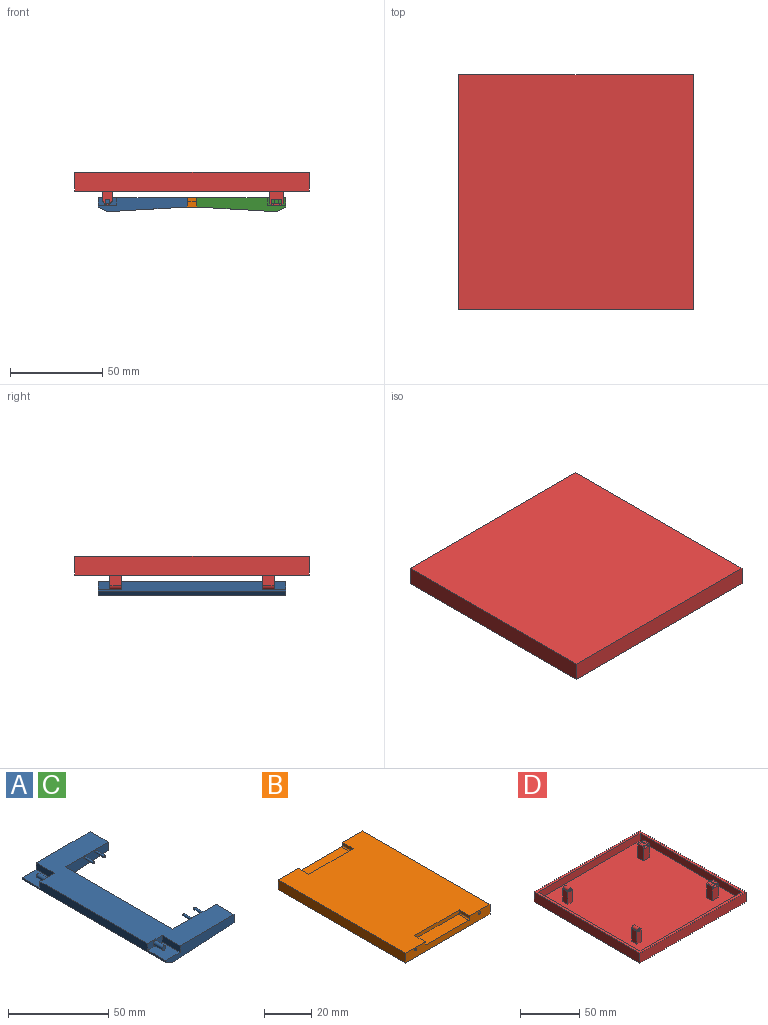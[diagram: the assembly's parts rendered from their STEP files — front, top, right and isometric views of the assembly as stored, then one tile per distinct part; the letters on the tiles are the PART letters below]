
ASSEMBLY  parts=4 mates=4
PART A: 29 faces, bbox 48.3x101.6x7.6 mm
  f0: plane 101.6x48.26mm, normal (0,0,1), area 2322.6mm2, adj f1,f2,f3,f4,f6,f8,f9,f10
  f1: plane 101.6x5.08mm, normal (-1,0,0), area 412.9mm2, adj f0,f2,f3,f7,f12,f13,f21,f22
  f2: plane 48.26x7.62mm, normal (0,1,0), area 265.2mm2, adj f0,f1,f5,f6,f7,f20,f21
  f3: plane 48.26x7.62mm, normal (0,-1,0), area 265.2mm2, adj f0,f1,f4,f5,f7,f11,f12
  f4: plane 12.7x5.08mm, normal (1,0,0), area 64.5mm2, adj f0,f3,f5,f8
  f5: plane 101.6x43.18mm, normal (0.06,0,-1), area 2068.1mm2, adj f2,f3,f4,f6,f7,f8,f9,f10
  f6: plane 12.7x5.08mm, normal (1,0,0), area 64.5mm2, adj f0,f2,f5,f9
  f7: plane 101.6x5.08mm, normal (-0.45,0,-0.89), area 577mm2, adj f1,f2,f3,f5
  f8: plane 30.48x6.87mm, normal (0,1,0), area 179.6mm2, adj f0,f4,f5,f10,f25,f27
  f9: plane 30.48x6.87mm, normal (0,-1,0), area 179.6mm2, adj f0,f5,f6,f10,f16,f18
  f10: plane 76.2x6.87mm, normal (1,0,0), area 523.7mm2, adj f0,f5,f8,f9
  f11: plane 12.7x4.06mm, normal (-1,0,0), area 51.6mm2, adj f0,f3,f12,f13
  f12: plane 12.7x10.16mm, normal (0,0,1), area 129mm2, adj f1,f3,f11,f13
  f13: plane 10.16x4.06mm, normal (0,-1,0), area 36.2mm2, adj f0,f1,f11,f12,f14
  f14: cylinder r=1.27mm len=6.35mm, axis (0,1,0), area 50.7mm2, adj f13,f15
  f15: plane 2.54x2.54mm, normal (0,-1,0), area 5.1mm2, adj f14
  f16: cylinder r=0.64mm len=6.35mm, axis (0,1,0), area 25.3mm2, adj f9,f17
  f17: plane 1.27x1.27mm, normal (0,-1,0), area 1.3mm2, adj f16
  f18: cylinder r=0.64mm len=6.35mm, axis (0,1,0), area 25.3mm2, adj f9,f19
  f19: plane 1.27x1.27mm, normal (0,-1,0), area 1.3mm2, adj f18
  f20: plane 12.7x4.06mm, normal (-1,0,0), area 51.6mm2, adj f0,f2,f21,f22
  f21: plane 12.7x10.16mm, normal (0,0,1), area 129mm2, adj f1,f2,f20,f22
  f22: plane 10.16x4.06mm, normal (0,1,0), area 36.2mm2, adj f0,f1,f20,f21,f23
  f23: cylinder r=1.27mm len=6.35mm, axis (0,-1,0), area 50.7mm2, adj f22,f24
  f24: plane 2.54x2.54mm, normal (0,1,0), area 5.1mm2, adj f23
  f25: cylinder r=0.64mm len=6.35mm, axis (0,-1,0), area 25.3mm2, adj f8,f26
  f26: plane 1.27x1.27mm, normal (0,1,0), area 1.3mm2, adj f25
  f27: cylinder r=0.64mm len=6.35mm, axis (0,-1,0), area 25.3mm2, adj f8,f28
  f28: plane 1.27x1.27mm, normal (0,1,0), area 1.3mm2, adj f27
PART B: 26 faces, bbox 50.8x76.2x5.1 mm
  f0: plane 50.8x5.08mm, normal (0,1,0), area 204.9mm2, adj f2,f3,f4,f5,f16,f17,f18,f19
  f1: plane 50.8x5.08mm, normal (0,-1,0), area 204.9mm2, adj f2,f3,f4,f5,f6,f7,f8,f9
  f2: plane 76.2x50.8mm, normal (0,0,-1), area 3871mm2, adj f0,f1,f3,f5
  f3: plane 76.2x5.08mm, normal (1,0,0), area 387.1mm2, adj f0,f1,f2,f4
  f4: plane 76.2x50.8mm, normal (0,0,1), area 3532.3mm2, adj f0,f1,f3,f5,f6,f10,f11,f16
  f5: plane 76.2x5.08mm, normal (-1,0,0), area 387.1mm2, adj f0,f1,f2,f4
  f6: plane 6.35x1.27mm, normal (1,0,0), area 8.1mm2, adj f1,f4,f7,f11
  f7: cylinder r=0.64mm len=6.35mm, axis (0,-1,0), area 6.3mm2, adj f1,f6,f8,f11
  f8: plane 25.4x6.35mm, normal (0,0,1), area 161.3mm2, adj f1,f7,f9,f11
  f9: cylinder r=0.64mm len=6.35mm, axis (0,-1,0), area 6.3mm2, adj f1,f8,f10,f11
  f10: plane 6.35x1.27mm, normal (-1,0,0), area 8.1mm2, adj f1,f4,f9,f11
  f11: plane 26.67x1.91mm, normal (0,-1,0), area 50.6mm2, adj f4,f6,f7,f8,f9,f10
  f12: cylinder r=0.64mm len=6.35mm, axis (0,-1,0), area 25.3mm2, adj f1,f13
  f13: plane 1.27x1.27mm, normal (0,-1,0), area 1.3mm2, adj f12
  f14: cylinder r=0.64mm len=6.35mm, axis (0,-1,0), area 25.3mm2, adj f1,f15
  f15: plane 1.27x1.27mm, normal (0,-1,0), area 1.3mm2, adj f14
  f16: plane 6.35x1.27mm, normal (1,0,0), area 8.1mm2, adj f0,f4,f20,f21
  f17: plane 6.35x1.27mm, normal (-1,0,0), area 8.1mm2, adj f0,f4,f18,f21
  f18: cylinder r=0.64mm len=6.35mm, axis (0,1,0), area 6.3mm2, adj f0,f17,f19,f21
  f19: plane 25.4x6.35mm, normal (0,0,1), area 161.3mm2, adj f0,f18,f20,f21
  f20: cylinder r=0.64mm len=6.35mm, axis (0,1,0), area 6.3mm2, adj f0,f16,f19,f21
  f21: plane 26.67x1.91mm, normal (0,1,0), area 50.6mm2, adj f4,f16,f17,f18,f19,f20
  f22: cylinder r=0.64mm len=6.35mm, axis (0,1,0), area 25.3mm2, adj f0,f23
  f23: plane 1.27x1.27mm, normal (0,1,0), area 1.3mm2, adj f22
  f24: cylinder r=0.64mm len=6.35mm, axis (0,1,0), area 25.3mm2, adj f0,f25
  f25: plane 1.27x1.27mm, normal (0,1,0), area 1.3mm2, adj f24
PART C: same geometry as A
PART D: 53 faces, bbox 127x127x17.8 mm
  f0: plane 14.48x6.35mm, normal (-1,0,0), area 91.9mm2, adj f1,f11,f40,f50
  f1: plane 15.24x7.62mm, normal (0,-1,0), area 101.2mm2, adj f0,f4,f5,f11,f41,f42,f43,f44
  f2: plane 15.24x5.08mm, normal (0,1,0), area 68.5mm2, adj f11,f38,f39,f47,f48,f49,f52
  f3: plane 15.24x5.08mm, normal (0,-1,0), area 68.5mm2, adj f11,f38,f39,f47,f48,f49,f52
  f4: plane 14.48x6.35mm, normal (1,0,0), area 91.9mm2, adj f1,f11,f40,f41
  f5: plane 6.35x0.81mm, normal (0,0,1), area 5.1mm2, adj f1,f40,f42,f51
  f6: plane 15.24x5.08mm, normal (0,1,0), area 68.5mm2, adj f11,f22,f23,f32,f33,f34,f37
  f7: plane 15.24x5.08mm, normal (0,-1,0), area 68.5mm2, adj f11,f22,f23,f32,f33,f34,f37
  f8: plane 15.24x7.62mm, normal (0,1,0), area 101.2mm2, adj f9,f11,f24,f25,f26,f27,f28,f29
  f9: plane 6.35x0.81mm, normal (0,0,1), area 5.1mm2, adj f8,f10,f27,f36
  f10: plane 15.24x7.62mm, normal (0,-1,0), area 101.2mm2, adj f9,f11,f24,f25,f26,f27,f28,f29
  f11: plane 121.92x121.92mm, normal (0,0,1), area 14703.2mm2, adj f0,f1,f2,f3,f4,f6,f7,f8
  f12: plane 127x10.16mm, normal (0,-1,0), area 1290.3mm2, adj f13,f15,f16,f21
  f13: plane 127x10.16mm, normal (1,0,0), area 1290.3mm2, adj f12,f14,f16,f21
  f14: plane 127x10.16mm, normal (0,1,0), area 1290.3mm2, adj f13,f15,f16,f21
  f15: plane 127x10.16mm, normal (-1,0,0), area 1290.3mm2, adj f12,f14,f16,f21
  f16: plane 127x127mm, normal (0,0,-1), area 16129mm2, adj f12,f13,f14,f15
  f17: plane 121.92x7.62mm, normal (-1,0,0), area 929mm2, adj f11,f18,f20,f21
  f18: plane 121.92x7.62mm, normal (0,1,0), area 929mm2, adj f11,f17,f19,f21
  f19: plane 121.92x7.62mm, normal (1,0,0), area 929mm2, adj f11,f18,f20,f21
  f20: plane 121.92x7.62mm, normal (0,-1,0), area 929mm2, adj f11,f17,f19,f21
  f21: plane 127x127mm, normal (0,0,1), area 1264.5mm2, adj f12,f13,f14,f15,f17,f18,f19,f20
  f22: plane 13.21x6.35mm, normal (1,0,0), area 83.9mm2, adj f6,f7,f11,f37
  f23: plane 13.21x6.35mm, normal (-1,0,0), area 83.9mm2, adj f6,f7,f11,f32
  f24: plane 14.48x6.35mm, normal (1,0,0), area 91.9mm2, adj f8,f10,f11,f26
  f25: plane 14.48x6.35mm, normal (-1,0,0), area 91.9mm2, adj f8,f10,f11,f35
  f26: plane 6.35x0.19mm, normal (0,0,1), area 1.2mm2, adj f8,f10,f24,f27
  f27: cylinder r=8.89mm len=6.35mm, axis (0,-1,0), area 21.1mm2, adj f8,f9,f10,f26
  f28: plane 6.35x5.08mm, normal (0,0,1), area 32.3mm2, adj f8,f10,f29,f31
  f29: plane 6.35x2.54mm, normal (-1,0,0), area 16.1mm2, adj f8,f10,f28,f30
  f30: plane 6.35x5.08mm, normal (0,0,-1), area 32.3mm2, adj f8,f10,f29,f31
  f31: plane 6.35x2.54mm, normal (1,0,0), area 16.1mm2, adj f8,f10,f28,f30
  f32: plane 6.35x0.51mm, normal (0,0,1), area 3.2mm2, adj f6,f7,f23,f33
  f33: cylinder r=2.03mm len=6.35mm, axis (0,-1,0), area 40.5mm2, adj f6,f7,f32,f37
  f34: cylinder r=1.27mm len=6.35mm, axis (0,-1,0), area 50.7mm2, adj f6,f7
  f35: plane 6.35x0.19mm, normal (0,0,1), area 1.2mm2, adj f8,f10,f25,f36
  f36: cylinder r=8.89mm len=6.35mm, axis (0,-1,0), area 21.1mm2, adj f8,f9,f10,f35
  f37: plane 6.35x0.51mm, normal (0,0,1), area 3.2mm2, adj f6,f7,f22,f33
  f38: plane 13.21x6.35mm, normal (1,0,0), area 83.9mm2, adj f2,f3,f11,f52
  f39: plane 13.21x6.35mm, normal (-1,0,0), area 83.9mm2, adj f2,f3,f11,f47
  f40: plane 15.24x7.62mm, normal (0,1,0), area 101.2mm2, adj f0,f4,f5,f11,f41,f42,f43,f44
  f41: plane 6.35x0.19mm, normal (0,0,1), area 1.2mm2, adj f1,f4,f40,f42
  f42: cylinder r=8.89mm len=6.35mm, axis (0,1,0), area 21.1mm2, adj f1,f5,f40,f41
  f43: plane 6.35x5.08mm, normal (0,0,1), area 32.3mm2, adj f1,f40,f44,f46
  f44: plane 6.35x2.54mm, normal (1,0,0), area 16.1mm2, adj f1,f40,f43,f45
  f45: plane 6.35x5.08mm, normal (0,0,-1), area 32.3mm2, adj f1,f40,f44,f46
  f46: plane 6.35x2.54mm, normal (-1,0,0), area 16.1mm2, adj f1,f40,f43,f45
  f47: plane 6.35x0.51mm, normal (0,0,1), area 3.2mm2, adj f2,f3,f39,f48
  f48: cylinder r=2.03mm len=6.35mm, axis (0,1,0), area 40.5mm2, adj f2,f3,f47,f52
  f49: cylinder r=1.27mm len=6.35mm, axis (0,1,0), area 50.7mm2, adj f2,f3
  f50: plane 6.35x0.19mm, normal (0,0,1), area 1.2mm2, adj f0,f1,f40,f51
  f51: cylinder r=8.89mm len=6.35mm, axis (0,1,0), area 21.1mm2, adj f1,f5,f40,f50
  f52: plane 6.35x0.51mm, normal (0,0,1), area 3.2mm2, adj f2,f3,f38,f48
PLACE A rot(axis=(0.04,0.03,-1),0deg) t=(-0.15,-0.08,2.37)mm
PLACE B t=(-0.15,-0.08,0)mm fixed
PLACE C rot(axis=(0,0,-1),180deg) t=(-0.15,-0.08,2.37)mm
PLACE D rot(axis=(1,0,0),180deg) t=(-0.15,-0.08,16.26)mm
MATE revolute B.f14 <-> A.f25  axis (0,-1,0) through (-19.2,-38.18,1.27)mm
MATE revolute D.f48 <-> A.f14  axis (0,1,0) through (-45.87,-38.18,0.51)mm
MATE pin_slot C.f14 <-> D.f40  axis (0,-1,0) through (45.57,-44.53,0.51)mm
MATE revolute B.f12 <-> C.f16  axis (0,-1,0) through (18.9,-38.18,1.27)mm
